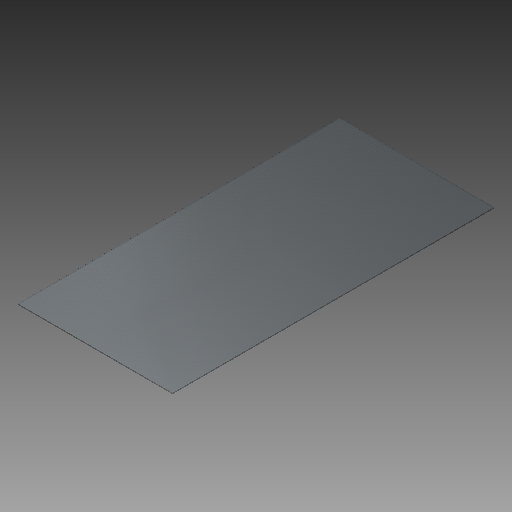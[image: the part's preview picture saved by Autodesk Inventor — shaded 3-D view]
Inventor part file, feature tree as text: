
AUTODESK INVENTOR PART (.ipt)
format: ipt  version: 2018 (Build 220112000, 112)  size: 130,560 bytes
history: native  units: mm
features: extrude x1, sketch x1
ambient origin geometry x8: Origin, YZ Plane, XZ Plane, XY Plane, X Axis, Y Axis, Z Axis, Center Point
bodies: Volumenkörper1 (feature_tree)
feature tree (2):
  extrude  "Extrusion1"  Depth=224.5mm
  sketch  "Skizze1"  dims[d0=108.0mm d1=224.5mm d2=0.8mm d3=0.0mm]
